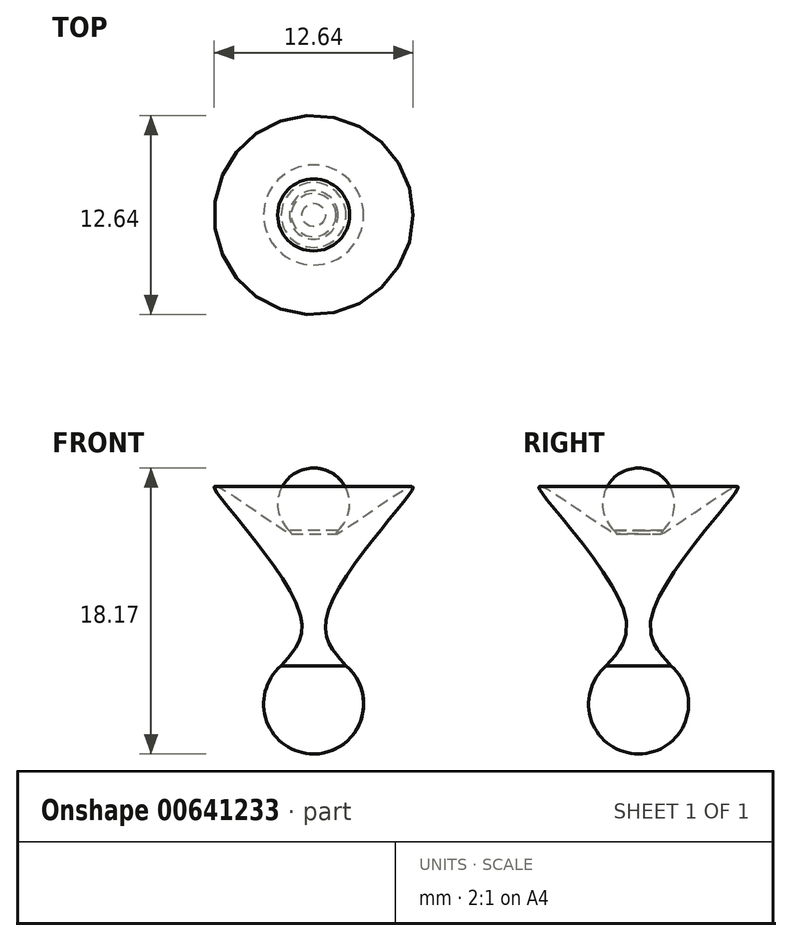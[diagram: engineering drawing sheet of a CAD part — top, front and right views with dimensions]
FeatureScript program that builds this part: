
annotation { "Feature Type Name" : "Feature", "Feature Type Description" : "" }
export const myFeature = defineFeature(function(context is Context, id is Id, definition is map)
    precondition{}
    {
        {
            var Q0;
            Q0=qCreatedBy(makeId("Front.planeOp"),FACE);
            var sketch = newSketch(context, id + "F0", { "sketchPlane" : qUnion([Q0])});
            skCircle(sketch, "E0", {"center": v(0, 0) * mm, "radius": 3.18 * mm});
            skCircle(sketch, "E1", {"center": v(0, 12.7) * mm, "radius": 2.29 * mm});
            skFitSpline(sketch, "E2", {"points": [v(1.54, 11.01) * mm, v(1.44, 10.87) * mm, v(1.4, 10.8) * mm, v(2.5, 11.45) * mm, v(6.32, 13.78) * mm, v(0.78, 5.36) * mm, v(2.06, 2.41) * mm], "startDerivative": vector(-4.15, -5.87) * mm, "endDerivative": vector(5, -7.25) * mm});
            skLineSegment(sketch, "E3", {"start": v(0, 14.99) * mm, "end": v(0, -3.17) * mm});
            skSolve(sketch);
        }
        {
            var Q0;
            {var subQ0=sQuery(id+"F0.wireOp",EDGE,"E1");var subQ1=makeQuery(id+"F0.imprint","INTERSECT",VERTEX,{"derivedFrom":[subQ0,sQuery(id+"F0.wireOp",EDGE,"E2")]});Q0=makeQuery(id+"F0.imprint","IMPRINT",FACE,{"disambiguationData":[TD([[makeQuery(id+"F0.imprint","IMPRINT",EDGE,{"disambiguationData":[TD([[subQ1,1.0]])],"derivedFrom":subQ0}),1.0]])]});}
            var Q1;
            {var subQ0=sQuery(id+"F0.wireOp",EDGE,"E2");Q1=makeQuery(id+"F0.imprint","IMPRINT",FACE,{"disambiguationData":[TD([[makeQuery(id+"F0.imprint","IMPRINT",EDGE,{"derivedFrom":subQ0}),-1.0]])]});}
            var Q2;
            {var subQ0=sQuery(id+"F0.wireOp",EDGE,"E0");var subQ1=makeQuery(id+"F0.imprint","INTERSECT",VERTEX,{"derivedFrom":[subQ0,sQuery(id+"F0.wireOp",EDGE,"E2")]});Q2=makeQuery(id+"F0.imprint","IMPRINT",FACE,{"disambiguationData":[TD([[makeQuery(id+"F0.imprint","IMPRINT",EDGE,{"disambiguationData":[TD([[subQ1,-1.0]])],"derivedFrom":subQ0}),1.0]])]});}
            var Q3;
            Q3=sQuery(id+"F0.wireOp",EDGE,"E3");
            revolve(context, id + "F1", {"entities" : qUnion([Q0, Q1, Q2]), "axis" : qUnion([Q3]), "revolveType" : RevolveType.FULL});
        }
    });
